# Revit family: Advance-Tabco_Floor_Trough_two_outlet_8563
name_source: partatom
category: Plumbing Fixtures
revit_build: Autodesk Revit 2015 (Build: 20140322_1515(x64)
units: mm (PartAtom-declared; Revit-internal decimal feet)

## types (9) — shared parameters
Trench Depth = 0' - 4"
zero-valued in all types: WFU

## per-type parameters (varying)
| type | Drain Centerlines | Grate Support | Grate Width | Grating Spacing | Trough Length | Trough Width |
| 18W x 120L | 3' - 4" | 9' - 9 3/4" | 1' - 3 3/4" | 118 | 10' - 0" | 1' - 6" |
| 18W x 108L | 3' - 0" | 8' - 9 3/4" | 1' - 3 3/4" | 106 | 9' - 0" | 1' - 6" |
| 18W x 96L | 2' - 8" | 7' - 9 3/4" | 1' - 3 3/4" | 94 | 8' - 0" | 1' - 6" |
| 12W x 96L | 2' - 8" | 7' - 9 3/4" | 0' - 9 3/4" | 94 | 8' - 0" | 1' - 0" |
| 12W x 108L | 3' - 0" | 8' - 9 3/4" | 0' - 9 3/4" | 106 | 9' - 0" | 1' - 0" |
| 12W x 120L | 3' - 4" | 9' - 9 3/4" | 0' - 9 3/4" | 118 | 10' - 0" | 1' - 0" |
| 24W x 96L | 3' - 4" | 9' - 9 3/4" | 1' - 9 3/4" | 118 | 10' - 0" | 2' - 0" |
| 24W x 108L | 3' - 0" | 8' - 9 3/4" | 1' - 9 3/4" | 106 | 9' - 0" | 2' - 0" |
| 24W x 120L | 3' - 4" | 9' - 9 3/4" | 1' - 9 3/4" | 118 | 10' - 0" | 2' - 0" |

## geometry (parser evidence)
native form markers: Sweep x3
no freeform markers — native parametric forms only
